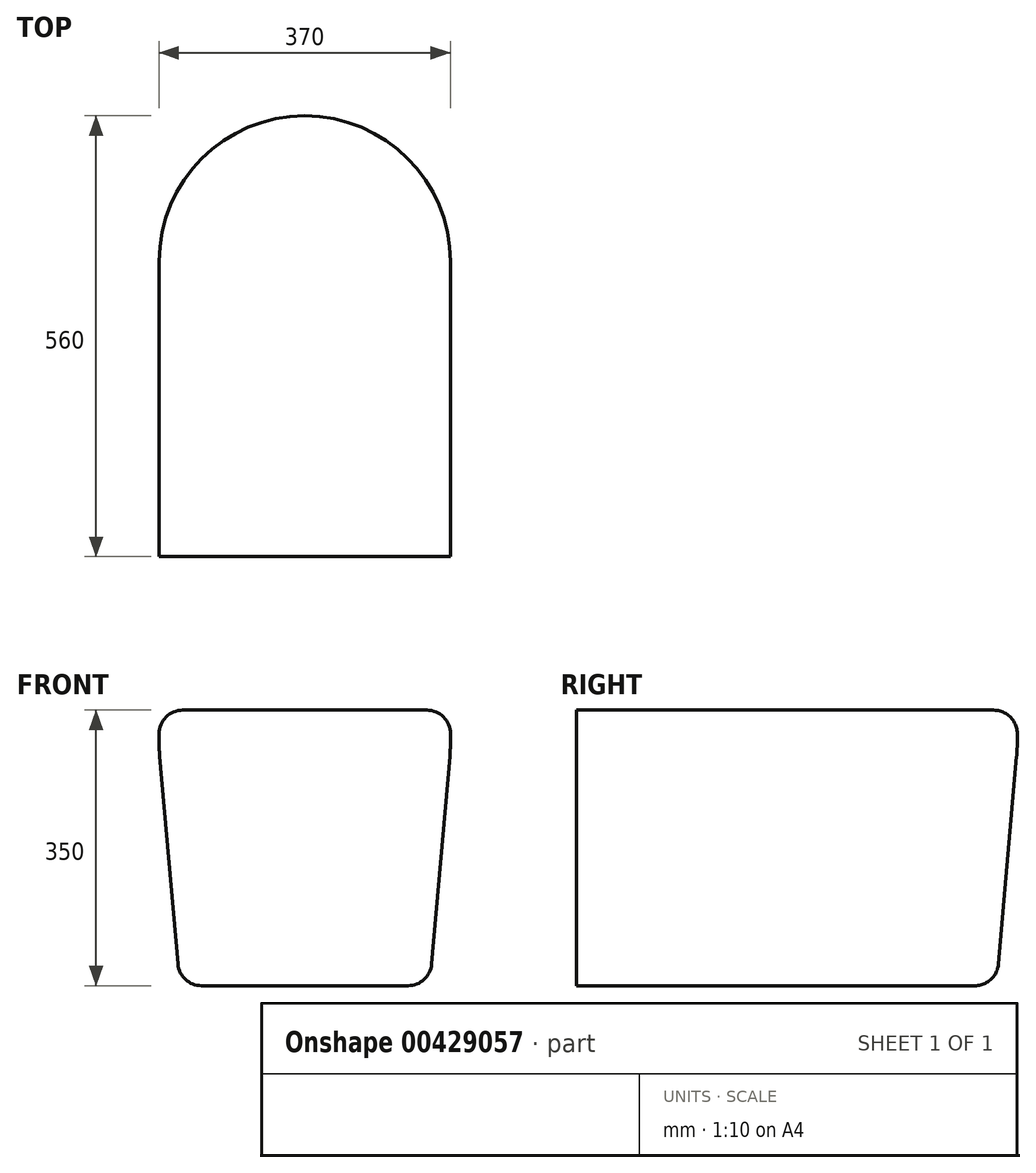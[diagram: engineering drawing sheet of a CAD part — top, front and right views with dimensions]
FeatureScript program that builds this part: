
annotation { "Feature Type Name" : "Feature", "Feature Type Description" : "" }
export const myFeature = defineFeature(function(context is Context, id is Id, definition is map)
    precondition{}
    {
        {
            var Q0;
            Q0=qCreatedBy(makeId("Top.planeOp"),FACE);
            var sketch = newSketch(context, id + "F0", { "sketchPlane" : qUnion([Q0])});
            skLineSegment(sketch, "E0.bottom", {"start": v(-185, 0) * mm, "end": v(185, 0) * mm});
            skLineSegment(sketch, "E0.top", {"start": v(0, 560) * mm, "end": v(0, 560) * mm});
            skLineSegment(sketch, "E0.left", {"start": v(-185, 0) * mm, "end": v(-185, 375) * mm});
            skLineSegment(sketch, "E0.right", {"start": v(185, 0) * mm, "end": v(185, 375) * mm});
            skPoint(sketch, "E1.visualSharp", {"position": v(-185, 560) * mm});
            skArc(sketch, "E1.filletArc", {"start": v(0, 560) * mm, "mid": v(-130.81, 505.81) * mm, "end": v(-185, 375) * mm});
            skPoint(sketch, "E2.visualSharp", {"position": v(185, 560) * mm});
            skArc(sketch, "E2.filletArc", {"start": v(185, 375) * mm, "mid": v(130.81, 505.81) * mm, "end": v(0, 560) * mm});
            skSolve(sketch);
        }
        {
            var Q0;
            Q0=makeQuery(id+"F0.imprint","IMPRINT",FACE,{"disambiguationData":[TD([[makeQuery(id+"F0.imprint","IMPRINT",EDGE,{"derivedFrom":sQuery(id+"F0.wireOp",EDGE,"E0.bottom")}),1.0]])]});
            extrude(context, id + "F1", {"entities" : qUnion([Q0]), "depth" : 350 * mm});
        }
        {
            var Q0;
            Q0=makeQuery(id+"F1.opExtrude","CAP_EDGE",EDGE,{"disambiguationData":[OSD([sQuery(id+"F0.wireOp",EDGE,"E0.right")])],"isStart":true});
            var Q1;
            Q1=makeQuery(id+"F1.opExtrude","CAP_EDGE",EDGE,{"disambiguationData":[OSD([sQuery(id+"F0.wireOp",EDGE,"E1.filletArc"),sQuery(id+"F0.wireOp",EDGE,"E2.filletArc")])],"isStart":true});
            var Q2;
            Q2=makeQuery(id+"F1.opExtrude","CAP_EDGE",EDGE,{"disambiguationData":[OSD([sQuery(id+"F0.wireOp",EDGE,"E0.left")])],"isStart":true});
            chamfer(context, id + "F2", {"entities" : qUnion([Q0, Q1, Q2]), "chamferType" : ChamferType.OFFSET_ANGLE, "width" : 300 * mm, "oppositeDirection" : false, "angle" : 5 * degree, "tangentPropagation" : true});
        }
        {
            var Q0;
            {var subQ0=sQuery(id+"F0.wireOp",EDGE,"E2.filletArc");var subQ1=sQuery(id+"F0.wireOp",EDGE,"E1.filletArc");Q0=makeQuery(id+"F2.opChamfer","BLEND_EDGE",EDGE,{"blendedFrom":[makeQuery(id+"F1.opExtrude","CAP_EDGE",EDGE,{"disambiguationData":[OSD([subQ1,subQ0])],"isStart":true}),makeQuery(id+"F1.opExtrude","SWEPT_FACE",FACE,{"disambiguationData":[OSD([subQ1,subQ0])]})],"blendedInto":[makeQuery(id+"F1.opExtrude","SWEPT_FACE",FACE,{"disambiguationData":[OSD([subQ1,subQ0])]})]});}
            var Q1;
            {var subQ0=sQuery(id+"F0.wireOp",EDGE,"E0.left");Q1=makeQuery(id+"F2.opChamfer","BLEND_EDGE",EDGE,{"blendedFrom":[makeQuery(id+"F1.opExtrude","CAP_EDGE",EDGE,{"disambiguationData":[OSD([subQ0])],"isStart":true}),makeQuery(id+"F1.opExtrude","SWEPT_FACE",FACE,{"disambiguationData":[OSD([subQ0])]})],"blendedInto":[makeQuery(id+"F1.opExtrude","SWEPT_FACE",FACE,{"disambiguationData":[OSD([subQ0])]})]});}
            var Q2;
            {var subQ0=sQuery(id+"F0.wireOp",EDGE,"E0.right");Q2=makeQuery(id+"F2.opChamfer","BLEND_EDGE",EDGE,{"blendedFrom":[makeQuery(id+"F1.opExtrude","CAP_EDGE",EDGE,{"disambiguationData":[OSD([subQ0])],"isStart":true}),makeQuery(id+"F1.opExtrude","SWEPT_FACE",FACE,{"disambiguationData":[OSD([subQ0])]})],"blendedInto":[makeQuery(id+"F1.opExtrude","SWEPT_FACE",FACE,{"disambiguationData":[OSD([subQ0])]})]});}
            fillet(context, id + "F3", {"entities" : qUnion([Q0, Q1, Q2]), "radius" : 200 * mm, "tangentPropagation" : true, "allowEdgeOverflow" : false});
        }
        {
            var Q0;
            {var subQ0=sQuery(id+"F0.wireOp",EDGE,"E0.right");Q0=makeQuery(id+"F2.opChamfer","BLEND_EDGE",EDGE,{"blendedFrom":[makeQuery(id+"F1.opExtrude","CAP_EDGE",EDGE,{"disambiguationData":[OSD([subQ0])],"isStart":true}),makeQuery(id+"F1.opExtrude","CAP_FACE",FACE,{"disambiguationData":[OSD([sQuery(id+"F0.wireOp",EDGE,"E0.bottom"),sQuery(id+"F0.wireOp",EDGE,"E0.left"),subQ0,sQuery(id+"F0.wireOp",EDGE,"E1.filletArc"),sQuery(id+"F0.wireOp",EDGE,"E2.filletArc")])],"isStart":true})],"blendedInto":[makeQuery(id+"F1.opExtrude","CAP_FACE",FACE,{"disambiguationData":[OSD([sQuery(id+"F0.wireOp",EDGE,"E0.bottom"),sQuery(id+"F0.wireOp",EDGE,"E0.left"),subQ0,sQuery(id+"F0.wireOp",EDGE,"E1.filletArc"),sQuery(id+"F0.wireOp",EDGE,"E2.filletArc")])],"isStart":true})]});}
            var Q1;
            {var subQ0=sQuery(id+"F0.wireOp",EDGE,"E2.filletArc");var subQ1=sQuery(id+"F0.wireOp",EDGE,"E1.filletArc");Q1=makeQuery(id+"F2.opChamfer","BLEND_EDGE",EDGE,{"blendedFrom":[makeQuery(id+"F1.opExtrude","CAP_EDGE",EDGE,{"disambiguationData":[OSD([subQ1,subQ0])],"isStart":true}),makeQuery(id+"F1.opExtrude","CAP_FACE",FACE,{"disambiguationData":[OSD([sQuery(id+"F0.wireOp",EDGE,"E0.bottom"),sQuery(id+"F0.wireOp",EDGE,"E0.left"),sQuery(id+"F0.wireOp",EDGE,"E0.right"),subQ1,subQ0])],"isStart":true})],"blendedInto":[makeQuery(id+"F1.opExtrude","CAP_FACE",FACE,{"disambiguationData":[OSD([sQuery(id+"F0.wireOp",EDGE,"E0.bottom"),sQuery(id+"F0.wireOp",EDGE,"E0.left"),sQuery(id+"F0.wireOp",EDGE,"E0.right"),subQ1,subQ0])],"isStart":true})]});}
            var Q2;
            {var subQ0=sQuery(id+"F0.wireOp",EDGE,"E0.left");Q2=makeQuery(id+"F2.opChamfer","BLEND_EDGE",EDGE,{"blendedFrom":[makeQuery(id+"F1.opExtrude","CAP_EDGE",EDGE,{"disambiguationData":[OSD([subQ0])],"isStart":true}),makeQuery(id+"F1.opExtrude","CAP_FACE",FACE,{"disambiguationData":[OSD([sQuery(id+"F0.wireOp",EDGE,"E0.bottom"),subQ0,sQuery(id+"F0.wireOp",EDGE,"E0.right"),sQuery(id+"F0.wireOp",EDGE,"E1.filletArc"),sQuery(id+"F0.wireOp",EDGE,"E2.filletArc")])],"isStart":true})],"blendedInto":[makeQuery(id+"F1.opExtrude","CAP_FACE",FACE,{"disambiguationData":[OSD([sQuery(id+"F0.wireOp",EDGE,"E0.bottom"),subQ0,sQuery(id+"F0.wireOp",EDGE,"E0.right"),sQuery(id+"F0.wireOp",EDGE,"E1.filletArc"),sQuery(id+"F0.wireOp",EDGE,"E2.filletArc")])],"isStart":true})]});}
            var Q3;
            Q3=makeQuery(id+"F1.opExtrude","CAP_EDGE",EDGE,{"disambiguationData":[OSD([sQuery(id+"F0.wireOp",EDGE,"E0.right")])],"isStart":false});
            var Q4;
            Q4=makeQuery(id+"F1.opExtrude","CAP_EDGE",EDGE,{"disambiguationData":[OSD([sQuery(id+"F0.wireOp",EDGE,"E1.filletArc"),sQuery(id+"F0.wireOp",EDGE,"E2.filletArc")])],"isStart":false});
            var Q5;
            Q5=makeQuery(id+"F1.opExtrude","CAP_EDGE",EDGE,{"disambiguationData":[OSD([sQuery(id+"F0.wireOp",EDGE,"E0.left")])],"isStart":false});
            fillet(context, id + "F4", {"entities" : qUnion([Q0, Q1, Q2, Q3, Q4, Q5]), "radius" : 30 * mm, "tangentPropagation" : true, "allowEdgeOverflow" : false});
        }
    });
